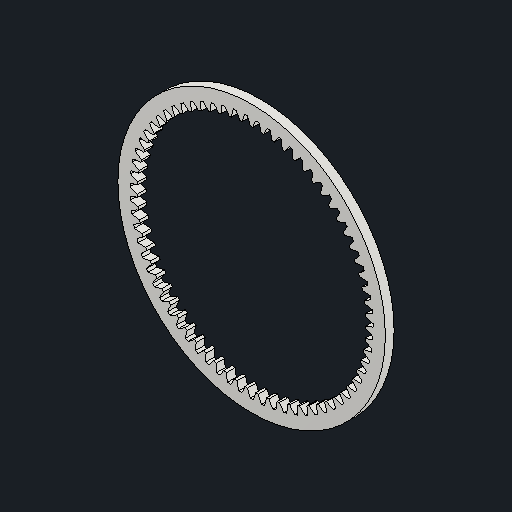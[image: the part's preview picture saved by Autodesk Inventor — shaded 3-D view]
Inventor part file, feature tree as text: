
AUTODESK INVENTOR PART (.ipt)
format: ipt  version: 2023.2 (Build 272271030, 271C)  size: 394,752 bytes
history: native  units: mm (DEFAULTED — no unit token found)
features: plane x3, other x3, sketch x2, extrude x1
ambient origin geometry x8: Origin, YZ Plane, XZ Plane, XY Plane, X Axis, Y Axis, Z Axis, Center Point
bodies: Solid1 (feature_tree)
feature tree (9):
  extrude  "Extrusion1"  Depth=5.0mm TaperAngle=0.0deg
  plane  "Work Plane2"
  plane  "Work Plane8"
  plane  "Work Plane9"
  other  "Spur Gear"
  sketch  "Sketch1"  dims[d0=152.9mm d1=5.0mm d2=0.0mm]
  sketch  "Sketch2"  dims[d3=134.0mm d4=10.0mm d5=0.0mm d16=51.0mm d17=0.0mm d34=0.468894mm d39=0.0mm d45=0.0mm d47=51.0mm d50=0.0mm d51=0.0mm d52=51.0mm]
  other  "Srf1"
  other  "Pitch Diameter"
